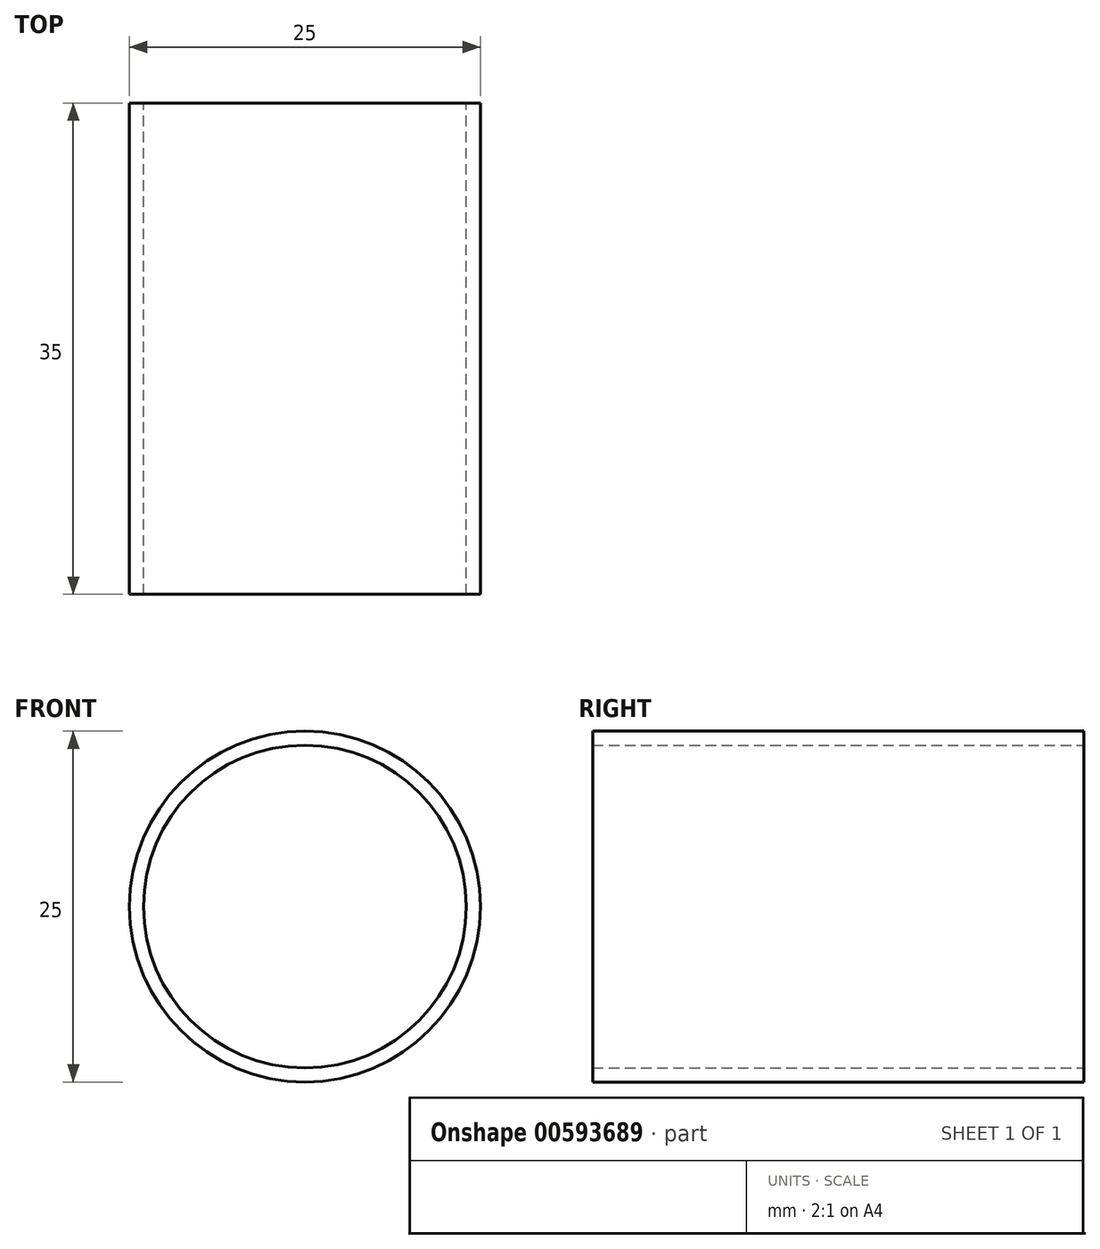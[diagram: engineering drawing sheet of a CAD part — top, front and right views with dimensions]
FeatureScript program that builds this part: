
annotation { "Feature Type Name" : "Feature", "Feature Type Description" : "" }
export const myFeature = defineFeature(function(context is Context, id is Id, definition is map)
    precondition{}
    {
        {
            var Q0;
            Q0=qCreatedBy(makeId("Front.planeOp"),FACE);
            var sketch = newSketch(context, id + "F0", { "sketchPlane" : qUnion([Q0])});
            skCircle(sketch, "E0", {"center": v(0, 0) * mm, "radius": 12.5 * mm});
            skCircle(sketch, "E1", {"center": v(0, 0) * mm, "radius": 11.5 * mm});
            skSolve(sketch);
        }
        {
            var Q0;
            Q0 = qSketchRegion(id + "F0", true);
            extrude(context, id + "F1", {"entities" : qUnion([Q0]), "depth" : 35 * mm, "offsetDistance" : 25.4 * mm});
        }
    });
